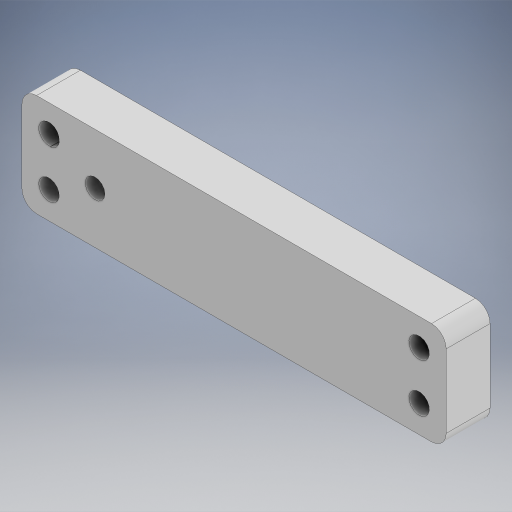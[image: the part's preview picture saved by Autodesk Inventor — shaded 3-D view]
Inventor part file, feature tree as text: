
AUTODESK INVENTOR PART (.ipt)
format: ipt  version: 2024 (Build 280153000, 153)  size: 330,752 bytes
history: native  units: mm
features: other x5, sketch x5, reference x5, projected_geometry x5, extrude x4, hole x1, fillet x1
ambient origin geometry x8: Origin, YZ Plane, XZ Plane, XY Plane, X Axis, Y Axis, Z Axis, Center Point
bodies: Body1 (feature_tree)
feature tree (26):
  other  "솔리드1"
  other  "작업 평면1"
  extrude  "돌출1"  Depth=0.3mm
  extrude  "돌출2"  Depth=4.0mm
  hole  "구멍1"  [1 undecoded]
  fillet  "모깎기1"  Radius=0.3mm
  extrude  "돌출3"  Depth=3.0mm TaperAngle=0.0deg
  extrude  "돌출4"  Depth=2.0mm
  sketch  "스케치1"
  reference  "참조1"
  sketch  "스케치2"
  projected_geometry  "투영된 루프1"
  reference  "참조2"
  reference  "참조3"
  reference  "참조4"
  reference  "참조5"
  sketch  "스케치3"
  projected_geometry  "투영된 루프2"
  sketch  "스케치4"
  projected_geometry  "투영된 루프3"
  sketch  "스케치5"
  projected_geometry  "투영된 루프4"
  projected_geometry  "투영된 루프5"
  other  "<userpath>\Desktop\ZIG\조립품1.iam"
  other  "조립품1.iam"
  other  "body_top:1"
note: 1 required parameter value undecoded (feature->parameter linkage not recoverable at this tier; creation-order binding heuristic only, values carry confidence <= 0.55)
